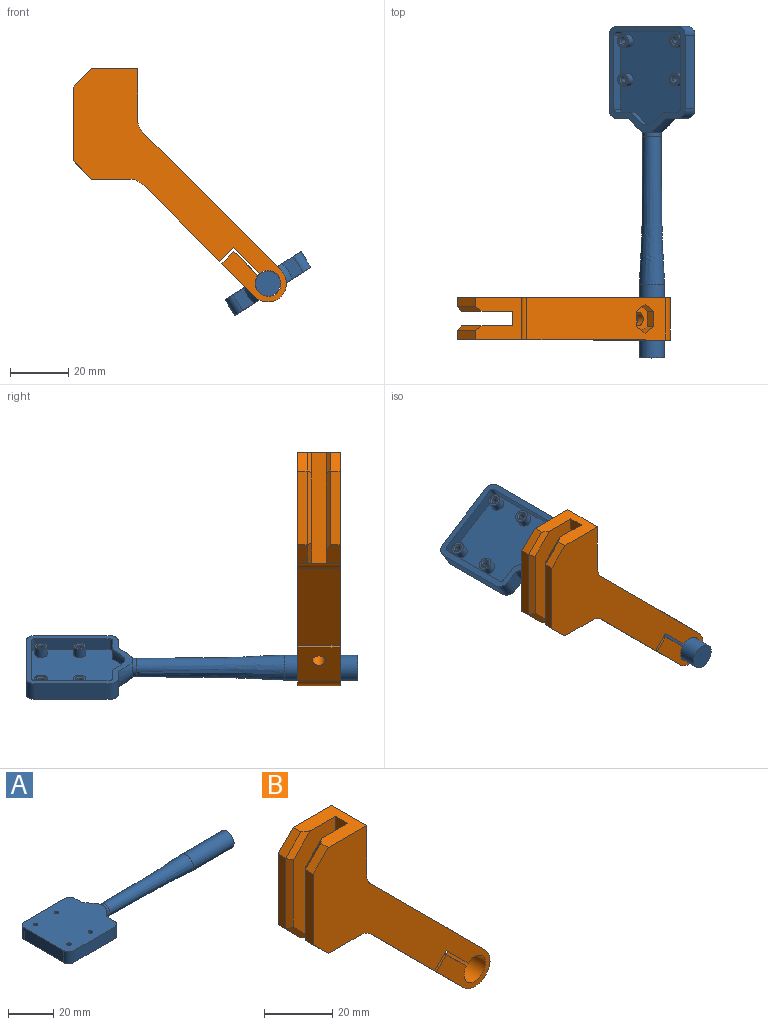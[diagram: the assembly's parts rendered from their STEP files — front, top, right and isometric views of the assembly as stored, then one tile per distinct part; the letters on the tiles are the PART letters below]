
ASSEMBLY  parts=2 mates=1
PART A: 48 faces, bbox 118.3x35x20.5 mm
  f0: plane 36.83x31mm, normal (0,0,-1), area 239.5mm2, adj f1,f2,f3,f4,f5,f8,f9,f10
  f1: plane 6.35x4.71mm, normal (1,0,0), area 27.2mm2, adj f0,f6,f8,f13
  f2: plane 6.35x4.71mm, normal (1,0,0), area 27.2mm2, adj f0,f6,f9,f10
  f3: plane 25.4x6.35mm, normal (0,1,0), area 161.3mm2, adj f0,f6,f10,f11
  f4: plane 24.65x6.35mm, normal (-1,0,0), area 156.5mm2, adj f0,f6,f11,f12
  f5: plane 25.4x6.35mm, normal (0,-1,0), area 161.3mm2, adj f0,f6,f12,f13
  f6: plane 36.83x31mm, normal (0,0,1), area 1010.6mm2, adj f1,f2,f3,f4,f5,f8,f9,f10
  f7: cylinder r=3.17mm len=6.35mm, axis (-1,0,0), area 25.3mm2, adj f8,f9,f14
  f8: cone r=3.17mm half-angle=45deg, axis (-1,0,0), area 49.9mm2, adj f0,f1,f6,f7
  f9: cone r=3.17mm half-angle=45deg, axis (-1,0,0), area 49.9mm2, adj f0,f2,f6,f7
  f10: cylinder r=3.17mm len=6.35mm, axis (0,0,1), area 31.7mm2, adj f0,f2,f3,f6
  f11: cylinder r=3.17mm len=6.35mm, axis (0,0,-1), area 31.7mm2, adj f0,f3,f4,f6
  f12: cylinder r=3.17mm len=6.35mm, axis (0,0,1), area 31.7mm2, adj f0,f4,f5,f6
  f13: cylinder r=3.17mm len=6.35mm, axis (0,0,-1), area 31.7mm2, adj f0,f1,f5,f6
  f14: bspline ~50.8x8.64mm, area 1123.4mm2, adj f7,f15
  f15: cylinder r=4.32mm len=25.4mm, axis (-1,0,0), area 689.1mm2, adj f14,f16
  f16: plane 8.64x8.64mm, normal (1,0,0), area 58.6mm2, adj f15
  f17: plane 5.61x4.35mm, normal (-1,0,0), area 22.1mm2, adj f0,f22,f24,f28
  f18: plane 5.61x4.35mm, normal (-1,0,0), area 22.1mm2, adj f0,f22,f24,f25
  f19: plane 25.4x4.35mm, normal (0,-1,0), area 110.5mm2, adj f0,f22,f25,f26
  f20: plane 24.65x4.35mm, normal (1,0,0), area 107.2mm2, adj f0,f22,f26,f27
  f21: plane 25.4x4.35mm, normal (0,1,0), area 110.5mm2, adj f0,f22,f27,f28
  f22: plane 34x27mm, normal (0,0,-1), area 740.1mm2, adj f17,f18,f19,f20,f21,f24,f25,f26
  f23: cylinder r=1.18mm len=2.35mm, axis (-1,0,0), area 15.5mm2, adj f24,f29
  f24: cone r=1.76mm half-angle=45deg, axis (-1,0,0), area 83mm2, adj f0,f17,f18,f22,f23
  f25: cylinder r=1.18mm len=4.35mm, axis (0,0,1), area 8mm2, adj f0,f18,f19,f22
  f26: cylinder r=1.18mm len=4.35mm, axis (0,0,-1), area 8mm2, adj f0,f19,f20,f22
  f27: cylinder r=1.18mm len=4.35mm, axis (0,0,1), area 8mm2, adj f0,f20,f21,f22
  f28: cylinder r=1.18mm len=4.35mm, axis (0,0,-1), area 8mm2, adj f0,f17,f21,f22
  f29: offset ~54.8x12.64mm, area 485.3mm2, adj f23,f30
  f30: cylinder r=2.32mm len=23.4mm, axis (-1,0,0), area 340.8mm2, adj f29,f31
  f31: plane 4.64x4.64mm, normal (-1,0,0), area 16.9mm2, adj f30
  f32: cylinder r=0.97mm len=4.85mm, axis (0,0,1), area 29.4mm2, adj f6,f47
  f33: cylinder r=2.17mm len=4.33mm, axis (0,0,1), area 45.6mm2, adj f22,f34
  f34: plane 4.33x4.33mm, normal (0,0,-1), area 7.9mm2, adj f33,f47
  f35: cylinder r=0.97mm len=4.85mm, axis (0,0,1), area 29.4mm2, adj f6,f44
  f36: cylinder r=2.17mm len=4.33mm, axis (0,0,1), area 45.6mm2, adj f22,f37
  f37: plane 4.33x4.33mm, normal (0,0,-1), area 7.9mm2, adj f36,f44
  f38: cylinder r=0.97mm len=4.85mm, axis (0,0,1), area 29.4mm2, adj f6,f46
  f39: cylinder r=2.17mm len=4.33mm, axis (0,0,1), area 45.6mm2, adj f22,f40
  f40: plane 4.33x4.33mm, normal (0,0,-1), area 7.9mm2, adj f39,f46
  f41: cylinder r=0.97mm len=4.85mm, axis (0,0,1), area 29.4mm2, adj f6,f45
  f42: cylinder r=2.17mm len=4.33mm, axis (0,0,1), area 45.6mm2, adj f22,f43
  f43: plane 4.33x4.33mm, normal (0,0,-1), area 7.9mm2, adj f42,f45
  f44: cone r=0.97mm half-angle=45deg, axis (0,0,-1), area 5.5mm2, adj f35,f37
  f45: cone r=0.97mm half-angle=45deg, axis (0,0,-1), area 5.5mm2, adj f41,f43
  f46: cone r=0.97mm half-angle=45deg, axis (0,0,-1), area 5.5mm2, adj f38,f40
  f47: cone r=0.97mm half-angle=45deg, axis (0,0,-1), area 5.5mm2, adj f32,f34
PART B: 39 faces, bbox 73.5x14.5x80.4 mm
  f0: cylinder r=2.29mm len=5.12mm, axis (-0.71,0,-0.71), area 38.3mm2, adj f29,f38
  f1: plane 26.45x26.45mm, normal (-0.71,0,-0.71), area 543.9mm2, adj f5,f6,f26,f30
  f2: cylinder r=4.45mm len=14.54mm, axis (0,-1,0), area 391.3mm2, adj f5,f6,f27,f29
  f3: plane 17.51x14.54mm, normal (1,0,0), area 254.6mm2, adj f5,f6,f11,f25
  f4: plane 25.4x3.18mm, normal (-1,0,0), area 80.6mm2, adj f5,f13,f15,f20
  f5: plane 80.37x73.48mm, normal (0,-1,0), area 1597.1mm2, adj f1,f2,f3,f4,f11,f12,f13,f15
  f6: plane 80.37x73.48mm, normal (0,1,0), area 1597.1mm2, adj f1,f2,f3,f7,f11,f12,f14,f16
  f7: plane 25.4x3.18mm, normal (-1,0,0), area 80.6mm2, adj f6,f14,f16,f18
  f8: plane 38.1x17.46mm, normal (0,-1,0), area 616.2mm2, adj f9,f11,f12,f17,f18,f19
  f9: plane 38.1x5.02mm, normal (-1,0,0), area 191.1mm2, adj f8,f10,f11,f12
  f10: plane 38.1x17.46mm, normal (0,1,0), area 629.4mm2, adj f9,f11,f12,f13,f20,f21
  f11: plane 15.88x14.54mm, normal (0,0,1), area 163.6mm2, adj f3,f5,f6,f8,f9,f10,f15,f16
  f12: plane 14.54x13.24mm, normal (0,0,-1), area 127.1mm2, adj f5,f6,f8,f9,f10,f13,f14,f19
  f13: plane 6.35x6.35mm, normal (-0.71,0,-0.71), area 41mm2, adj f4,f5,f10,f12,f20
  f14: plane 6.35x6.35mm, normal (-0.71,0,-0.71), area 28.5mm2, adj f6,f7,f12,f19
  f15: plane 6.35x6.35mm, normal (-0.71,0,0.71), area 28.5mm2, adj f4,f5,f11,f21
  f16: plane 6.35x6.35mm, normal (-0.71,0,0.71), area 28.5mm2, adj f6,f7,f11,f17
  f17: plane 8.6x7.01mm, normal (-0.5,-0.71,0.5), area 21.2mm2, adj f8,f11,f16,f18
  f18: plane 25.4x1.59mm, normal (-0.71,-0.71,0), area 55.5mm2, adj f7,f8,f17,f19
  f19: plane 8.6x7.01mm, normal (-0.5,-0.71,-0.5), area 21.2mm2, adj f8,f12,f14,f18
  f20: plane 26.99x1.59mm, normal (-0.71,0.71,0), area 58.1mm2, adj f4,f10,f13,f21
  f21: plane 8.6x7.01mm, normal (-0.5,0.71,0.5), area 21.2mm2, adj f10,f11,f15,f20
  f22: plane 14.54x11.38mm, normal (-0.71,0,-0.71), area 217.7mm2, adj f5,f6,f24,f28,f31
  f23: plane 47.53x47.53mm, normal (0.71,0,0.71), area 911.4mm2, adj f5,f6,f24,f25,f32,f33,f34,f35
  f24: cylinder r=6.35mm len=14.54mm, axis (0,-1,0), area 290.1mm2, adj f5,f6,f22,f23
  f25: cylinder r=6.35mm len=14.54mm, axis (0,-1,0), area 72.5mm2, adj f3,f5,f6,f23
  f26: cylinder r=6.35mm len=14.54mm, axis (0,1,0), area 72.5mm2, adj f1,f5,f6,f12
  f27: plane 14.54x8.26mm, normal (0.71,0,0.71), area 153.5mm2, adj f2,f5,f6,f28,f31
  f28: plane 14.54x4.13mm, normal (-0.71,0,0.71), area 85mm2, adj f5,f6,f22,f27
  f29: plane 14.54x8.98mm, normal (-0.71,0,-0.71), area 168.3mm2, adj f0,f2,f5,f6,f30
  f30: plane 14.54x4.85mm, normal (0.71,0,-0.71), area 99.7mm2, adj f1,f5,f6,f29
  f31: cylinder r=2.29mm len=7.36mm, axis (-0.71,0,-0.71), area 83.9mm2, adj f22,f27
  f32: plane 5.04x2.25mm, normal (0.71,0,-0.71), area 16mm2, adj f23,f33,f37,f38
  f33: plane 5.33x5.33mm, normal (0.35,0.87,-0.35), area 16mm2, adj f23,f32,f34,f38
  f34: plane 5.33x5.33mm, normal (-0.35,0.87,0.35), area 16mm2, adj f23,f33,f35,f38
  f35: plane 5.04x2.25mm, normal (-0.71,0,0.71), area 16mm2, adj f23,f34,f36,f38
  f36: plane 5.33x5.33mm, normal (-0.35,-0.87,0.35), area 16mm2, adj f23,f35,f37,f38
  f37: plane 5.33x5.33mm, normal (0.35,-0.87,-0.35), area 16mm2, adj f23,f32,f36,f38
  f38: plane 10.09x6.18mm, normal (0.71,0,0.71), area 49.7mm2, adj f0,f32,f33,f34,f35,f36,f37
PLACE A rot(axis=(-0.69,0.69,-0.2),157.3deg) t=(28.64,99.72,-59.29)mm
PLACE B t=(-17.73,14.73,-26.05)mm fixed
MATE cylindrical A.f15 <-> B.f24  axis (0,1,0) through (30.34,1.29,-61.97)mm
